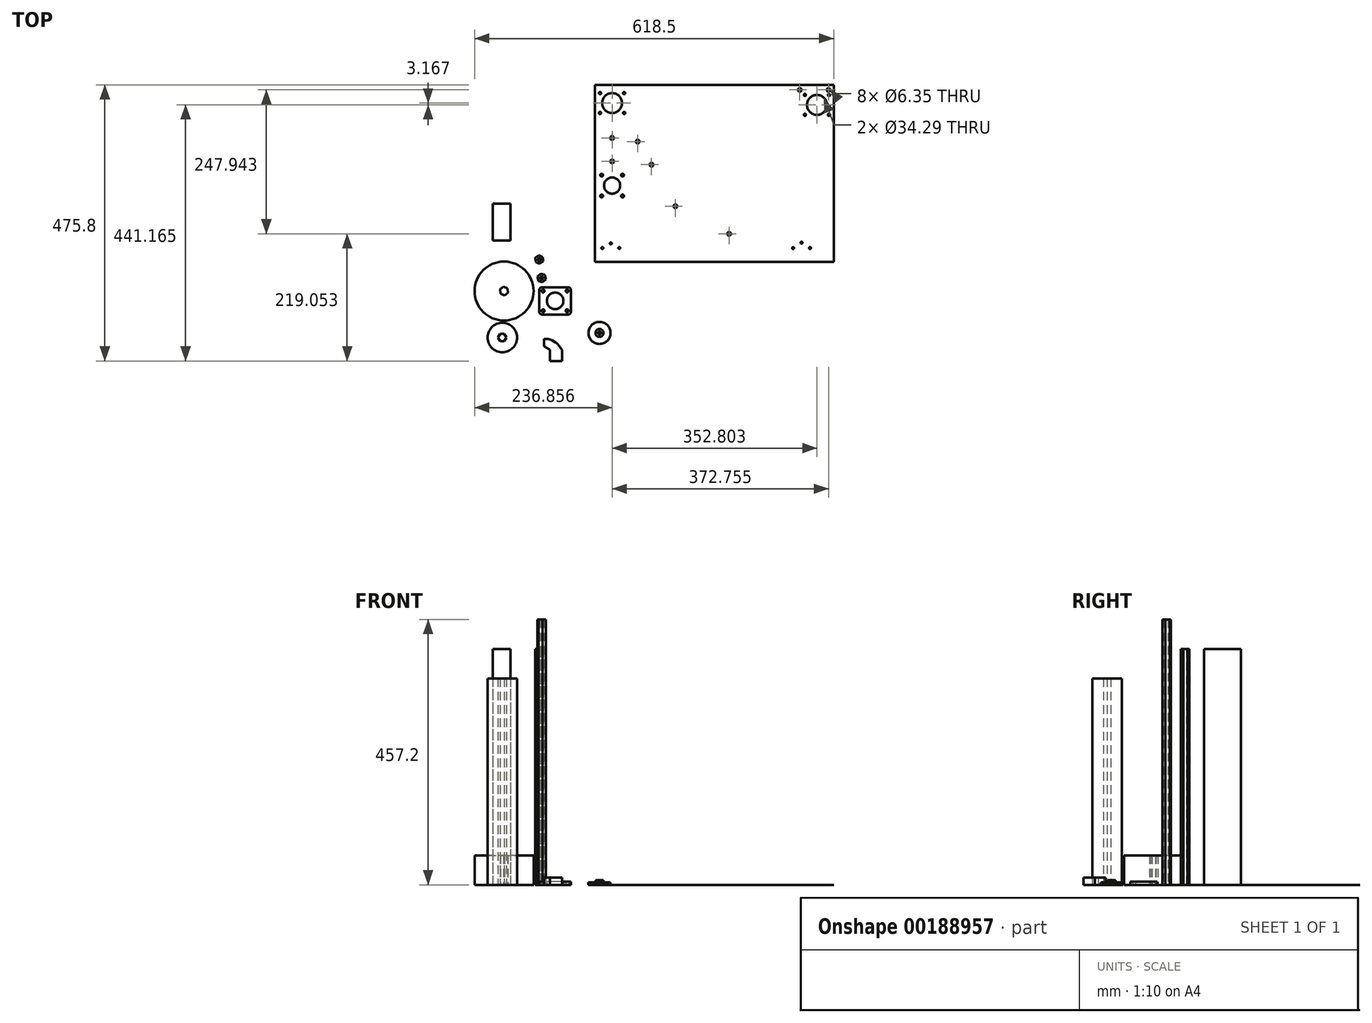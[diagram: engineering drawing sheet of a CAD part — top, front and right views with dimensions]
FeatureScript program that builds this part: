
annotation { "Feature Type Name" : "Feature", "Feature Type Description" : "" }
export const myFeature = defineFeature(function(context is Context, id is Id, definition is map)
    precondition{}
    {
        {
            assignVariable(context, id + "F0", {"name" : "width", "anyValue" : 406.4 * mm});
        }
        {
            var Q0;
            Q0=qCreatedBy(makeId("Top.planeOp"),FACE);
            var sketch = newSketch(context, id + "F1", { "sketchPlane" : qUnion([Q0])});
            skCircle(sketch, "E0", {"center": v(-143.52, 65.65) * mm, "radius": 50.8 * mm});
            skCircle(sketch, "E1.cCircle", {"center": v(-143.52, 65.65) * mm, "radius": 6.39 * mm, "construction": true});
            skLineSegment(sketch, "E1.0", {"start": v(-136.76, 62.7) * mm, "end": v(-142.7, 58.31) * mm});
            skLineSegment(sketch, "E1.1", {"start": v(-142.7, 58.31) * mm, "end": v(-149.46, 61.27) * mm});
            skLineSegment(sketch, "E1.2", {"start": v(-149.46, 61.27) * mm, "end": v(-150.28, 68.6) * mm});
            skLineSegment(sketch, "E1.3", {"start": v(-150.28, 68.6) * mm, "end": v(-144.34, 72.98) * mm});
            skLineSegment(sketch, "E1.4", {"start": v(-144.34, 72.98) * mm, "end": v(-137.58, 70.02) * mm});
            skLineSegment(sketch, "E1.5", {"start": v(-137.58, 70.02) * mm, "end": v(-136.76, 62.7) * mm});
            skPoint(sketch, "E1.0.midPoint", {"position": v(-139.73, 60.5) * mm});
            skCircle(sketch, "E2.cCircle", {"center": v(-78.77, 88.08) * mm, "radius": 6.55 * mm, "construction": true});
            skLineSegment(sketch, "E2.0", {"start": v(-71.5, 86) * mm, "end": v(-76.94, 80.75) * mm});
            skLineSegment(sketch, "E2.1", {"start": v(-76.94, 80.75) * mm, "end": v(-84.2, 82.83) * mm});
            skLineSegment(sketch, "E2.2", {"start": v(-84.2, 82.83) * mm, "end": v(-86.04, 90.16) * mm});
            skLineSegment(sketch, "E2.3", {"start": v(-86.04, 90.16) * mm, "end": v(-80.6, 95.41) * mm});
            skLineSegment(sketch, "E2.4", {"start": v(-80.6, 95.41) * mm, "end": v(-73.34, 93.33) * mm});
            skLineSegment(sketch, "E2.5", {"start": v(-73.34, 93.33) * mm, "end": v(-71.5, 86) * mm});
            skPoint(sketch, "E2.0.midPoint", {"position": v(-74.22, 83.37) * mm});
            skCircle(sketch, "E3", {"center": v(-78.77, 88.08) * mm, "radius": 2.55 * mm});
            skCircle(sketch, "E4.cCircle", {"center": v(-82.9, 119.76) * mm, "radius": 6.4 * mm, "construction": true});
            skLineSegment(sketch, "E4.0", {"start": v(-77.01, 124.21) * mm, "end": v(-76.1, 116.88) * mm});
            skLineSegment(sketch, "E4.1", {"start": v(-76.1, 116.88) * mm, "end": v(-82, 112.43) * mm});
            skLineSegment(sketch, "E4.2", {"start": v(-82, 112.43) * mm, "end": v(-88.8, 115.3) * mm});
            skLineSegment(sketch, "E4.3", {"start": v(-88.8, 115.3) * mm, "end": v(-89.71, 122.64) * mm});
            skLineSegment(sketch, "E4.4", {"start": v(-89.71, 122.64) * mm, "end": v(-83.82, 127.09) * mm});
            skLineSegment(sketch, "E4.5", {"start": v(-83.82, 127.09) * mm, "end": v(-77.01, 124.21) * mm});
            skPoint(sketch, "E4.0.midPoint", {"position": v(-76.56, 120.54) * mm});
            skCircle(sketch, "E5", {"center": v(-82.9, 119.76) * mm, "radius": 2.55 * mm});
            skCircle(sketch, "E6", {"center": v(-146.6, -14.5) * mm, "radius": 25.4 * mm});
            skCircle(sketch, "E7.cCircle", {"center": v(-146.6, -14.5) * mm, "radius": 6.35 * mm, "construction": true});
            skLineSegment(sketch, "E7.0", {"start": v(-142.93, -20.85) * mm, "end": v(-150.26, -20.85) * mm});
            skLineSegment(sketch, "E7.1", {"start": v(-150.26, -20.85) * mm, "end": v(-153.93, -14.5) * mm});
            skLineSegment(sketch, "E7.2", {"start": v(-153.93, -14.5) * mm, "end": v(-150.26, -8.15) * mm});
            skLineSegment(sketch, "E7.3", {"start": v(-150.26, -8.15) * mm, "end": v(-142.93, -8.15) * mm});
            skLineSegment(sketch, "E7.4", {"start": v(-142.93, -8.15) * mm, "end": v(-139.26, -14.5) * mm});
            skLineSegment(sketch, "E7.5", {"start": v(-139.26, -14.5) * mm, "end": v(-142.93, -20.85) * mm});
            skPoint(sketch, "E7.0.midPoint", {"position": v(-146.6, -20.85) * mm});
            skSolve(sketch);
        }
        {
            var Q0;
            Q0=makeQuery(id+"F1.imprint","IMPRINT",FACE,{"disambiguationData":[TD([[makeQuery(id+"F1.imprint","IMPRINT",EDGE,{"derivedFrom":sQuery(id+"F1.wireOp",EDGE,"E0")}),1.0]])]});
            extrude(context, id + "F2", {"entities" : qUnion([Q0]), "depth" : 50.8 * mm});
        }
        {
            var Q0;
            Q0=makeQuery(id+"F1.imprint","IMPRINT",FACE,{"disambiguationData":[TD([[makeQuery(id+"F1.imprint","IMPRINT",EDGE,{"derivedFrom":sQuery(id+"F1.wireOp",EDGE,"E2.0")}),-1.0]])]});
            extrude(context, id + "F3", {"entities" : qUnion([Q0]), "depth" : getVariable(context, 'width') + 50.8 * mm});
        }
        {
            var Q0;
            Q0=makeQuery(id+"F1.imprint","IMPRINT",FACE,{"disambiguationData":[TD([[makeQuery(id+"F1.imprint","IMPRINT",EDGE,{"derivedFrom":sQuery(id+"F1.wireOp",EDGE,"E4.0")}),-1.0]])]});
            extrude(context, id + "F4", {"entities" : qUnion([Q0]), "depth" : getVariable(context, 'width')});
        }
        {
            var Q0;
            Q0=qCreatedBy(makeId("Top.planeOp"),FACE);
            var sketch = newSketch(context, id + "F5", { "sketchPlane" : qUnion([Q0])});
            skLineSegment(sketch, "E8.bottom", {"start": v(-162.97, 216.04) * mm, "end": v(-132.49, 216.04) * mm});
            skLineSegment(sketch, "E8.top", {"start": v(-162.97, 152.54) * mm, "end": v(-132.49, 152.54) * mm});
            skLineSegment(sketch, "E8.left", {"start": v(-162.97, 216.04) * mm, "end": v(-162.97, 152.54) * mm});
            skLineSegment(sketch, "E8.right", {"start": v(-132.49, 216.04) * mm, "end": v(-132.49, 152.54) * mm});
            skLineSegment(sketch, "E9.bottom", {"start": v(12.7, 420.9) * mm, "end": v(424.18, 420.9) * mm});
            skLineSegment(sketch, "E9.top", {"start": v(12.7, 116.1) * mm, "end": v(424.18, 116.1) * mm});
            skLineSegment(sketch, "E9.left", {"start": v(12.7, 420.9) * mm, "end": v(12.7, 116.1) * mm});
            skLineSegment(sketch, "E9.right", {"start": v(424.18, 420.9) * mm, "end": v(424.18, 116.1) * mm});
            skCircle(sketch, "E10", {"center": v(395.34, 386.27) * mm, "radius": 17.15 * mm});
            skPoint(sketch, "E11.middle", {"position": v(42.54, 247.3) * mm});
            skCircle(sketch, "E12", {"center": v(365.67, 412.1) * mm, "radius": 3.18 * mm});
            skCircle(sketch, "E13", {"center": v(415.3, 412.1) * mm, "radius": 3.18 * mm});
            skLineSegment(sketch, "E14.bottom", {"start": v(374.6, 403.36) * mm, "end": v(416.08, 403.36) * mm, "construction": true});
            skLineSegment(sketch, "E14.top", {"start": v(374.6, 369.2) * mm, "end": v(416.08, 369.2) * mm, "construction": true});
            skLineSegment(sketch, "E14.left", {"start": v(374.6, 403.36) * mm, "end": v(374.6, 369.2) * mm, "construction": true});
            skLineSegment(sketch, "E14.right", {"start": v(416.08, 403.36) * mm, "end": v(416.08, 369.2) * mm, "construction": true});
            skCircle(sketch, "E15", {"center": v(374.6, 403.36) * mm, "radius": 1.9 * mm});
            skCircle(sketch, "E16", {"center": v(374.6, 369.2) * mm, "radius": 1.9 * mm});
            skCircle(sketch, "E17", {"center": v(416.08, 369.2) * mm, "radius": 1.9 * mm});
            skCircle(sketch, "E18", {"center": v(416.08, 403.36) * mm, "radius": 1.9 * mm});
            skCircle(sketch, "E19", {"center": v(54.9, 139.66) * mm, "radius": 1.65 * mm});
            skCircle(sketch, "E20", {"center": v(25.7, 139.66) * mm, "radius": 1.65 * mm});
            skCircle(sketch, "E21", {"center": v(40.3, 147.7) * mm, "radius": 1.65 * mm});
            skCircle(sketch, "E22", {"center": v(383.26, 139.66) * mm, "radius": 1.65 * mm});
            skCircle(sketch, "E23", {"center": v(354.06, 139.66) * mm, "radius": 1.65 * mm});
            skCircle(sketch, "E24", {"center": v(368.66, 149.07) * mm, "radius": 1.65 * mm});
            skCircle(sketch, "E25", {"center": v(42.54, 389.44) * mm, "radius": 17.15 * mm});
            skLineSegment(sketch, "E26", {"start": v(42.54, 389.44) * mm, "end": v(42.54, 405.95) * mm, "construction": true});
            skLineSegment(sketch, "E27.bottom", {"start": v(21.8, 406.52) * mm, "end": v(63.27, 406.52) * mm, "construction": true});
            skLineSegment(sketch, "E27.top", {"start": v(21.8, 372.36) * mm, "end": v(63.27, 372.36) * mm, "construction": true});
            skLineSegment(sketch, "E27.left", {"start": v(21.8, 406.52) * mm, "end": v(21.8, 372.36) * mm, "construction": true});
            skLineSegment(sketch, "E27.right", {"start": v(63.27, 406.52) * mm, "end": v(63.27, 372.36) * mm, "construction": true});
            skCircle(sketch, "E28", {"center": v(21.8, 406.52) * mm, "radius": 1.9 * mm});
            skCircle(sketch, "E29", {"center": v(21.8, 372.36) * mm, "radius": 1.9 * mm});
            skCircle(sketch, "E30", {"center": v(63.27, 372.36) * mm, "radius": 1.9 * mm});
            skCircle(sketch, "E31", {"center": v(63.27, 406.52) * mm, "radius": 1.9 * mm});
            skCircle(sketch, "E32", {"center": v(42.54, 247.3) * mm, "radius": 13.97 * mm});
            skCircle(sketch, "E33", {"center": v(42.54, 247.3) * mm, "radius": 25.4 * mm, "construction": true});
            skLineSegment(sketch, "E34.bottom", {"start": v(60.5, 229.35) * mm, "end": v(24.57, 229.35) * mm, "construction": true});
            skLineSegment(sketch, "E34.top", {"start": v(60.5, 265.27) * mm, "end": v(24.57, 265.27) * mm, "construction": true});
            skLineSegment(sketch, "E34.left", {"start": v(60.5, 229.35) * mm, "end": v(60.5, 265.27) * mm, "construction": true});
            skLineSegment(sketch, "E34.right", {"start": v(24.57, 229.35) * mm, "end": v(24.57, 265.27) * mm, "construction": true});
            skCircle(sketch, "E35", {"center": v(24.57, 229.35) * mm, "radius": 2.41 * mm});
            skCircle(sketch, "E36", {"center": v(24.57, 265.27) * mm, "radius": 2.41 * mm});
            skCircle(sketch, "E37", {"center": v(60.5, 265.27) * mm, "radius": 2.41 * mm});
            skCircle(sketch, "E38", {"center": v(60.5, 229.35) * mm, "radius": 2.41 * mm});
            skCircle(sketch, "E39", {"center": v(238.1, 355.84) * mm, "radius": 127 * mm, "construction": true});
            skCircle(sketch, "E40", {"center": v(244.07, 164.16) * mm, "radius": 3.18 * mm});
            skCircle(sketch, "E41", {"center": v(151.47, 211.72) * mm, "radius": 3.18 * mm});
            skCircle(sketch, "E42", {"center": v(110.37, 283.21) * mm, "radius": 3.18 * mm});
            skCircle(sketch, "E43", {"center": v(86.6, 323.11) * mm, "radius": 3.18 * mm});
            skLineSegment(sketch, "E44", {"start": v(424.18, 141.5) * mm, "end": v(336.76, 141.5) * mm, "construction": true});
            skLineSegment(sketch, "E45", {"start": v(318.08, 457.68) * mm, "end": v(249.84, 490.2) * mm, "construction": true});
            skCircle(sketch, "E46", {"center": v(42.54, 288.86) * mm, "radius": 3.18 * mm});
            skCircle(sketch, "E47", {"center": v(395.34, 386.27) * mm, "radius": 25.4 * mm, "construction": true});
            skCircle(sketch, "E48", {"center": v(42.54, 389.44) * mm, "radius": 50.8 * mm, "construction": true});
            skLineSegment(sketch, "E49", {"start": v(318.08, 457.68) * mm, "end": v(351.14, 409.16) * mm, "construction": true});
            skCircle(sketch, "E50", {"center": v(42.54, 329.26) * mm, "radius": 3.18 * mm});
            skPoint(sketch, "E51", {"position": v(410.43, 141.5) * mm});
            skLineSegment(sketch, "E52", {"start": v(410.43, 141.5) * mm, "end": v(395.34, 360.87) * mm, "construction": true});
            skSolve(sketch);
        }
        {
            var Q0;
            Q0=makeQuery(id+"F5.imprint","IMPRINT",FACE,{"disambiguationData":[TD([[makeQuery(id+"F5.imprint","IMPRINT",EDGE,{"derivedFrom":sQuery(id+"F5.wireOp",EDGE,"E8.bottom")}),-1.0]])]});
            extrude(context, id + "F6", {"entities" : qUnion([Q0]), "depth" : getVariable(context, 'width')});
        }
        {
            var Q0;
            Q0=makeQuery(id+"F5.imprint","IMPRINT",FACE,{"disambiguationData":[TD([[makeQuery(id+"F5.imprint","IMPRINT",EDGE,{"derivedFrom":sQuery(id+"F5.wireOp",EDGE,"E9.bottom")}),-1.0]])]});
            extrude(context, id + "F7", {"entities" : qUnion([Q0]), "depth" : 1 / 203.2 * mm});
        }
        {
            var Q0;
            Q0=qCreatedBy(makeId("Top.planeOp"),FACE);
            var sketch = newSketch(context, id + "F8", { "sketchPlane" : qUnion([Q0])});
            skLineSegment(sketch, "E53.bottom", {"start": v(-28.28, 25.21) * mm, "end": v(-82.9, 25.21) * mm});
            skLineSegment(sketch, "E53.top", {"start": v(-28.28, 72.2) * mm, "end": v(-82.9, 72.2) * mm});
            skLineSegment(sketch, "E53.left", {"start": v(-28.28, 25.21) * mm, "end": v(-28.28, 72.2) * mm});
            skLineSegment(sketch, "E53.right", {"start": v(-82.9, 25.21) * mm, "end": v(-82.9, 72.2) * mm});
            skPoint(sketch, "E53.middle", {"position": v(-55.59, 48.7) * mm});
            skCircle(sketch, "E54", {"center": v(-55.59, 48.7) * mm, "radius": 14.29 * mm});
            skLineSegment(sketch, "E55.bottom", {"start": v(-76.32, 65.8) * mm, "end": v(-34.85, 65.8) * mm, "construction": true});
            skLineSegment(sketch, "E55.top", {"start": v(-76.32, 31.62) * mm, "end": v(-34.85, 31.62) * mm, "construction": true});
            skLineSegment(sketch, "E55.left", {"start": v(-76.32, 65.8) * mm, "end": v(-76.32, 31.62) * mm, "construction": true});
            skLineSegment(sketch, "E55.right", {"start": v(-34.85, 65.8) * mm, "end": v(-34.85, 31.62) * mm, "construction": true});
            skCircle(sketch, "E56", {"center": v(-76.32, 65.8) * mm, "radius": 2.54 * mm});
            skCircle(sketch, "E57", {"center": v(-76.32, 31.62) * mm, "radius": 2.54 * mm});
            skCircle(sketch, "E58", {"center": v(-34.85, 31.62) * mm, "radius": 2.54 * mm});
            skCircle(sketch, "E59", {"center": v(-34.85, 65.8) * mm, "radius": 2.54 * mm});
            skSolve(sketch);
        }
        {
            var Q0;
            Q0 = qSketchRegion(id + "F8", true);
            extrude(context, id + "F9", {"entities" : qUnion([Q0]), "depth" : 5.5 * mm});
        }
        {
            var Q0;
            Q0=makeQuery(id+"F9.opExtrude","SWEPT_EDGE",EDGE,{"disambiguationData":[OSD([sQuery(id+"F8.wireOp",EDGE,"E53.bottom"),sQuery(id+"F8.wireOp",EDGE,"E53.left")])]});
            var Q1;
            Q1=makeQuery(id+"F9.opExtrude","SWEPT_EDGE",EDGE,{"disambiguationData":[OSD([sQuery(id+"F8.wireOp",EDGE,"E53.bottom"),sQuery(id+"F8.wireOp",EDGE,"E53.right")])]});
            var Q2;
            Q2=makeQuery(id+"F9.opExtrude","SWEPT_EDGE",EDGE,{"disambiguationData":[OSD([sQuery(id+"F8.wireOp",EDGE,"E53.top"),sQuery(id+"F8.wireOp",EDGE,"E53.left")])]});
            var Q3;
            Q3=makeQuery(id+"F9.opExtrude","SWEPT_EDGE",EDGE,{"disambiguationData":[OSD([sQuery(id+"F8.wireOp",EDGE,"E53.top"),sQuery(id+"F8.wireOp",EDGE,"E53.right")])]});
            fillet(context, id + "F10", {"entities" : qUnion([Q0, Q1, Q2, Q3]), "radius" : 5.08 * mm, "tangentPropagation" : true, "allowEdgeOverflow" : false});
        }
        {
            var Q0;
            Q0=makeQuery(id+"F1.imprint","IMPRINT",FACE,{"disambiguationData":[TD([[makeQuery(id+"F1.imprint","IMPRINT",EDGE,{"derivedFrom":sQuery(id+"F1.wireOp",EDGE,"E6")}),1.0]])]});
            extrude(context, id + "F11", {"entities" : qUnion([Q0]), "operationType" : NewBodyOperationType.ADD, "depth" : getVariable(context, 'width') - 50.8 * mm});
        }
        {
            var Q0;
            Q0=qCreatedBy(makeId("Top.planeOp"),FACE);
            var sketch = newSketch(context, id + "F12", { "sketchPlane" : qUnion([Q0])});
            skLineSegment(sketch, "E60", {"start": v(-64.23, -35.55) * mm, "end": v(-64.23, -54.9) * mm});
            skLineSegment(sketch, "E61", {"start": v(-64.23, -54.9) * mm, "end": v(-43.53, -54.9) * mm});
            skLineSegment(sketch, "E62", {"start": v(-43.53, -54.9) * mm, "end": v(-43.53, -35.68) * mm});
            skLineSegment(sketch, "E63", {"start": v(-43.53, -35.68) * mm, "end": v(-50.79, -26.31) * mm});
            skLineSegment(sketch, "E64", {"start": v(-54.4, -23.13) * mm, "end": v(-61.53, -18.95) * mm});
            skLineSegment(sketch, "E65", {"start": v(-67.95, -17.21) * mm, "end": v(-74.56, -17.21) * mm});
            skLineSegment(sketch, "E66", {"start": v(-74.56, -17.21) * mm, "end": v(-74.56, -29.88) * mm});
            skLineSegment(sketch, "E67", {"start": v(-74.56, -29.88) * mm, "end": v(-64.23, -35.55) * mm});
            skPoint(sketch, "E68.visualSharp", {"position": v(-64.5, -17.21) * mm});
            skArc(sketch, "E68.filletArc", {"start": v(-61.53, -18.95) * mm, "mid": v(-64.62, -17.65) * mm, "end": v(-67.95, -17.21) * mm});
            skPoint(sketch, "E69.visualSharp", {"position": v(-52.29, -24.37) * mm});
            skArc(sketch, "E69.filletArc", {"start": v(-50.79, -26.31) * mm, "mid": v(-52.44, -24.55) * mm, "end": v(-54.4, -23.13) * mm});
            skSolve(sketch);
        }
        {
            var Q0;
            Q0=makeQuery(id+"F12.imprint","IMPRINT",FACE,{"disambiguationData":[TD([[makeQuery(id+"F12.imprint","IMPRINT",EDGE,{"derivedFrom":sQuery(id+"F12.wireOp",EDGE,"E60")}),1.0]])]});
            extrude(context, id + "F13", {"entities" : qUnion([Q0]), "depth" : 12.7 * mm});
        }
        {
            var Q0;
            Q0=qCreatedBy(makeId("Top.planeOp"),FACE);
            var sketch = newSketch(context, id + "F14", { "sketchPlane" : qUnion([Q0])});
            skCircle(sketch, "E70", {"center": v(20.86, -6.52) * mm, "radius": 19.05 * mm});
            skCircle(sketch, "E71", {"center": v(20.86, -6.52) * mm, "radius": 6.88 * mm});
            skCircle(sketch, "E72", {"center": v(20.86, -6.52) * mm, "radius": 2.48 * mm});
            skSolve(sketch);
        }
        {
            var Q0;
            Q0=makeQuery(id+"F14.imprint","IMPRINT",FACE,{"disambiguationData":[TD([[makeQuery(id+"F14.imprint","IMPRINT",EDGE,{"derivedFrom":sQuery(id+"F14.wireOp",EDGE,"E70")}),1.0]])]});
            extrude(context, id + "F15", {"entities" : qUnion([Q0]), "depth" : 4.06 * mm});
        }
        {
            var Q0;
            Q0=makeQuery(id+"F14.imprint","IMPRINT",FACE,{"disambiguationData":[TD([[makeQuery(id+"F14.imprint","IMPRINT",EDGE,{"derivedFrom":sQuery(id+"F14.wireOp",EDGE,"E71")}),1.0]])]});
            extrude(context, id + "F16", {"entities" : qUnion([Q0]), "operationType" : NewBodyOperationType.ADD, "depth" : 8.04 * mm});
        }
    });
